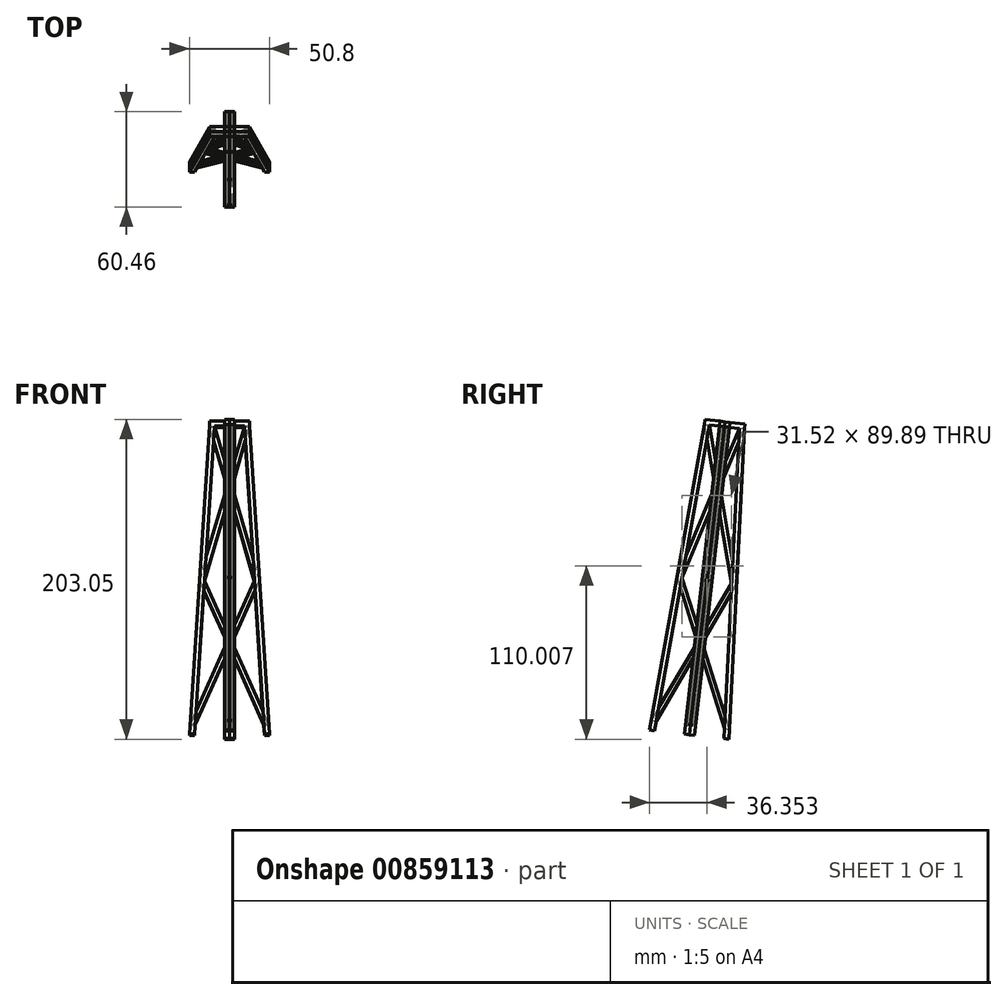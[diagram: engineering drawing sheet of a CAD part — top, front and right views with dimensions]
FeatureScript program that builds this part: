
annotation { "Feature Type Name" : "Feature", "Feature Type Description" : "" }
export const myFeature = defineFeature(function(context is Context, id is Id, definition is map)
    precondition{}
    {
        {
            var Q0;
            Q0=qCreatedBy(makeId("Top.planeOp"),FACE);
            var sketch = newSketch(context, id + "F0", { "sketchPlane" : qUnion([Q0])});
            skLineSegment(sketch, "E0", {"start": v(0, 0) * mm, "end": v(0, 116.82) * mm, "construction": true});
            skLineSegment(sketch, "E1", {"start": v(0, 0) * mm, "end": v(-140.82, 0) * mm, "construction": true});
            skSolve(sketch);
        }
        {
            var Q0;
            Q0=qCreatedBy(makeId("Right.planeOp"),FACE);
            var sketch = newSketch(context, id + "F1", { "sketchPlane" : qUnion([Q0])});
            skLineSegment(sketch, "E2", {"start": v(0, 0) * mm, "end": v(0, 190.5) * mm, "construction": true});
            skSolve(sketch);
        }
        {
            var Q0;
            Q0=qCreatedBy(makeId("Right.planeOp"),FACE);
            var sketch = newSketch(context, id + "F2", { "sketchPlane" : qUnion([Q0])});
            skPoint(sketch, "E3", {"position": v(-25.4, 0) * mm});
            skPoint(sketch, "E4.MirrorP", {"position": v(25.4, 0) * mm});
            skPoint(sketch, "E5", {"position": v(0, 215.9) * mm});
            skLineSegment(sketch, "E6", {"start": v(-25.4, 0) * mm, "end": v(0, 223.32) * mm, "construction": true});
            skSolve(sketch);
        }
        {
            var Q0;
            Q0 = qBodyType(qCreatedBy(id + "F2" ,EDGE), BodyType.WIRE);
            cPlane(context, id + "F3", {"entities" : qUnion([Q0]), "cplaneType" : CPlaneType.LINE_ANGLE, "offset" : 25.4 * mm, "angle" : 90 * degree, "oppositeDirection" : true, "width" : 152.4 * mm, "height" : 152.4 * mm});
        }
        {
            var Q0;
            Q0=qCreatedBy(id+"F3.planeOp",FACE);
            var sketch = newSketch(context, id + "F4", { "sketchPlane" : qUnion([Q0])});
            skPoint(sketch, "E7", {"position": v(-25.4, 0) * mm});
            skPoint(sketch, "E8", {"position": v(0, 215.9) * mm});
            skPoint(sketch, "E9", {"position": v(0, 196.85) * mm});
            skLineSegment(sketch, "E10", {"start": v(-25.4, 0) * mm, "end": v(-12.7, 196.85) * mm});
            skLineSegment(sketch, "E11.0", {"start": v(-22.22, 0) * mm, "end": v(-9.52, 196.85) * mm});
            skLineSegment(sketch, "E12", {"start": v(-25.4, 0) * mm, "end": v(-22.22, 0) * mm});
            skLineSegment(sketch, "E13", {"start": v(-12.7, 196.85) * mm, "end": v(-9.52, 196.85) * mm});
            skLineSegment(sketch, "E14", {"start": v(-12.7, 200.03) * mm, "end": v(-12.7, 196.85) * mm});
            skLineSegment(sketch, "E15.MirrorCS", {"start": v(12.7, 196.85) * mm, "end": v(9.52, 196.85) * mm});
            skLineSegment(sketch, "E16.MirrorCS", {"start": v(12.7, 200.03) * mm, "end": v(12.7, 196.85) * mm});
            skLineSegment(sketch, "E17.MirrorCS", {"start": v(25.4, 0) * mm, "end": v(22.22, 0) * mm});
            skLineSegment(sketch, "E18.MirrorCS", {"start": v(25.4, 0) * mm, "end": v(12.7, 196.85) * mm});
            skLineSegment(sketch, "E19.MirrorCS", {"start": v(22.22, 0) * mm, "end": v(9.52, 196.85) * mm});
            skLineSegment(sketch, "E20", {"start": v(-12.7, 196.85) * mm, "end": v(12.7, 196.85) * mm});
            skLineSegment(sketch, "E21", {"start": v(-12.7, 200.03) * mm, "end": v(12.7, 200.03) * mm});
            skLineSegment(sketch, "E22", {"start": v(-65.08, 200.03) * mm, "end": v(-65.08, 0) * mm, "construction": true});
            skLineSegment(sketch, "E23", {"start": v(-59.43, 196.85) * mm, "end": v(-59.43, 0) * mm, "construction": true});
            skLineSegment(sketch, "E24", {"start": v(-59.43, 98.43) * mm, "end": v(114.07, 98.43) * mm, "construction": true});
            skLineSegment(sketch, "E25", {"start": v(-44.46, 6.35) * mm, "end": v(-44.46, 0) * mm, "construction": true});
            skLineSegment(sketch, "E26", {"start": v(-25, 6.35) * mm, "end": v(15.87, 98.43) * mm});
            skLineSegment(sketch, "E27", {"start": v(15.87, 98.43) * mm, "end": v(19.05, 98.43) * mm});
            skLineSegment(sketch, "E28", {"start": v(19.05, 98.42) * mm, "end": v(-21.8, 6.35) * mm});
            skLineSegment(sketch, "E29", {"start": v(-21.8, 6.35) * mm, "end": v(-25, 6.35) * mm});
            skLineSegment(sketch, "E30", {"start": v(-9.52, 196.85) * mm, "end": v(19.05, 98.42) * mm});
            skLineSegment(sketch, "E31", {"start": v(15.87, 98.43) * mm, "end": v(-12.7, 196.85) * mm});
            skLineSegment(sketch, "E32", {"start": v(9.52, 196.85) * mm, "end": v(-19.05, 98.43) * mm});
            skLineSegment(sketch, "E33", {"start": v(-19.05, 98.43) * mm, "end": v(-15.88, 98.22) * mm});
            skLineSegment(sketch, "E34", {"start": v(-15.88, 98.22) * mm, "end": v(12.7, 196.85) * mm});
            skLineSegment(sketch, "E35", {"start": v(21.8, 6.35) * mm, "end": v(-19.05, 98.43) * mm});
            skLineSegment(sketch, "E36", {"start": v(-15.88, 98.22) * mm, "end": v(25, 6.35) * mm});
            skLineSegment(sketch, "E37", {"start": v(25, 6.35) * mm, "end": v(21.8, 6.35) * mm});
            skSolve(sketch);
        }
        {
            var Q0;
            {var subQ2=sQuery(id+"F4.wireOp",EDGE,"E12");Q0=makeQuery(id+"F4.imprint","IMPRINT",FACE,{"disambiguationData":[TD([[makeQuery(id+"F4.imprint","IMPRINT",EDGE,{"derivedFrom":subQ2}),1.0]])]});}
            var Q1;
            {var subQ0=sQuery(id+"F4.wireOp",EDGE,"E17.MirrorCS");Q1=makeQuery(id+"F4.imprint","IMPRINT",FACE,{"disambiguationData":[TD([[makeQuery(id+"F4.imprint","IMPRINT",EDGE,{"derivedFrom":subQ0}),-1.0]])]});}
            var Q2;
            {var subQ3=sQuery(id+"F4.wireOp",EDGE,"E26");var subQ5=sQuery(id+"F4.wireOp",EDGE,"E11.0");var subQ7=makeQuery(id+"F4.imprint","INTERSECT",VERTEX,{"derivedFrom":[subQ5,subQ3]});Q2=makeQuery(id+"F4.imprint","IMPRINT",FACE,{"disambiguationData":[TD([[makeQuery(id+"F4.imprint","IMPRINT",EDGE,{"disambiguationData":[TD([[subQ7,-1.0]])],"derivedFrom":subQ5}),1.0]])]});}
            var Q3;
            {var subQ0=sQuery(id+"F4.wireOp",EDGE,"E32");var subQ5=sQuery(id+"F4.wireOp",EDGE,"E11.0");var subQ6=makeQuery(id+"F4.imprint","INTERSECT",VERTEX,{"derivedFrom":[subQ5,subQ0]});Q3=makeQuery(id+"F4.imprint","IMPRINT",FACE,{"disambiguationData":[TD([[makeQuery(id+"F4.imprint","IMPRINT",EDGE,{"disambiguationData":[TD([[subQ6,-1.0]])],"derivedFrom":subQ5}),1.0]])]});}
            var Q4;
            {var subQ3=sQuery(id+"F4.wireOp",EDGE,"E29");Q4=makeQuery(id+"F4.imprint","IMPRINT",FACE,{"disambiguationData":[TD([[makeQuery(id+"F4.imprint","IMPRINT",EDGE,{"derivedFrom":subQ3}),-1.0]])]});}
            var Q5;
            {var subQ0=sQuery(id+"F4.wireOp",EDGE,"E33");Q5=makeQuery(id+"F4.imprint","IMPRINT",FACE,{"disambiguationData":[TD([[makeQuery(id+"F4.imprint","IMPRINT",EDGE,{"derivedFrom":subQ0}),-1.0]])]});}
            var Q6;
            {var subQ0=sQuery(id+"F4.wireOp",EDGE,"E33");Q6=makeQuery(id+"F4.imprint","IMPRINT",FACE,{"disambiguationData":[TD([[makeQuery(id+"F4.imprint","IMPRINT",EDGE,{"derivedFrom":subQ0}),1.0]])]});}
            var Q7;
            {var subQ5=sQuery(id+"F4.wireOp",EDGE,"E13");Q7=makeQuery(id+"F4.imprint","IMPRINT",FACE,{"disambiguationData":[TD([[makeQuery(id+"F4.imprint","IMPRINT",EDGE,{"derivedFrom":subQ5}),-1.0]])]});}
            var Q8;
            {var subQ3=sQuery(id+"F4.wireOp",EDGE,"E36");var subQ5=sQuery(id+"F4.wireOp",EDGE,"E19.MirrorCS");var subQ6=makeQuery(id+"F4.imprint","INTERSECT",VERTEX,{"derivedFrom":[subQ5,subQ3]});Q8=makeQuery(id+"F4.imprint","IMPRINT",FACE,{"disambiguationData":[TD([[makeQuery(id+"F4.imprint","IMPRINT",EDGE,{"disambiguationData":[TD([[subQ6,-1.0]])],"derivedFrom":subQ5}),-1.0]])]});}
            var Q9;
            {var subQ3=sQuery(id+"F4.wireOp",EDGE,"E30");var subQ5=sQuery(id+"F4.wireOp",EDGE,"E19.MirrorCS");var subQ6=makeQuery(id+"F4.imprint","INTERSECT",VERTEX,{"derivedFrom":[subQ5,subQ3]});Q9=makeQuery(id+"F4.imprint","IMPRINT",FACE,{"disambiguationData":[TD([[makeQuery(id+"F4.imprint","IMPRINT",EDGE,{"disambiguationData":[TD([[subQ6,-1.0]])],"derivedFrom":subQ5}),-1.0]])]});}
            var Q10;
            {var subQ3=sQuery(id+"F4.wireOp",EDGE,"E37");Q10=makeQuery(id+"F4.imprint","IMPRINT",FACE,{"disambiguationData":[TD([[makeQuery(id+"F4.imprint","IMPRINT",EDGE,{"derivedFrom":subQ3}),-1.0]])]});}
            var Q11;
            {var subQ0=sQuery(id+"F4.wireOp",EDGE,"E27");Q11=makeQuery(id+"F4.imprint","IMPRINT",FACE,{"disambiguationData":[TD([[makeQuery(id+"F4.imprint","IMPRINT",EDGE,{"derivedFrom":subQ0}),-1.0]])]});}
            var Q12;
            {var subQ0=sQuery(id+"F4.wireOp",EDGE,"E27");Q12=makeQuery(id+"F4.imprint","IMPRINT",FACE,{"disambiguationData":[TD([[makeQuery(id+"F4.imprint","IMPRINT",EDGE,{"derivedFrom":subQ0}),1.0]])]});}
            var Q13;
            {var subQ1=sQuery(id+"F4.wireOp",EDGE,"E13");Q13=makeQuery(id+"F4.imprint","IMPRINT",FACE,{"disambiguationData":[TD([[makeQuery(id+"F4.imprint","IMPRINT",EDGE,{"derivedFrom":subQ1}),1.0]])]});}
            var Q14;
            {var subQ0=sQuery(id+"F4.wireOp",EDGE,"E15.MirrorCS");Q14=makeQuery(id+"F4.imprint","IMPRINT",FACE,{"disambiguationData":[TD([[makeQuery(id+"F4.imprint","IMPRINT",EDGE,{"derivedFrom":subQ0}),1.0]])]});}
            extrude(context, id + "F5", {"entities" : qUnion([Q0, Q1, Q2, Q3, Q4, Q5, Q6, Q7, Q8, Q9, Q10, Q11, Q12, Q13, Q14]), "oppositeDirection" : true, "depth" : 3.17 * mm, "offsetDistance" : 25.4 * mm});
        }
        {
            var Q0;
            {var subQ5=sQuery(id+"F4.wireOp",EDGE,"E13");Q0=makeQuery(id+"F4.imprint","IMPRINT",FACE,{"disambiguationData":[TD([[makeQuery(id+"F4.imprint","IMPRINT",EDGE,{"derivedFrom":subQ5}),-1.0]])]});}
            var Q1;
            {var subQ3=sQuery(id+"F4.wireOp",EDGE,"E31");var subQ5=sQuery(id+"F4.wireOp",EDGE,"E32");var subQ6=makeQuery(id+"F4.imprint","INTERSECT",VERTEX,{"derivedFrom":[subQ3,subQ5]});Q1=makeQuery(id+"F4.imprint","IMPRINT",FACE,{"disambiguationData":[TD([[makeQuery(id+"F4.imprint","IMPRINT",EDGE,{"disambiguationData":[TD([[subQ6,-1.0]])],"derivedFrom":subQ3}),-1.0]])]});}
            var Q2;
            {var subQ0=sQuery(id+"F4.wireOp",EDGE,"E32");var subQ1=sQuery(id+"F4.wireOp",EDGE,"E19.MirrorCS");var subQ2=makeQuery(id+"F4.imprint","INTERSECT",VERTEX,{"derivedFrom":[subQ1,subQ0]});Q2=makeQuery(id+"F4.imprint","IMPRINT",FACE,{"disambiguationData":[TD([[makeQuery(id+"F4.imprint","IMPRINT",EDGE,{"disambiguationData":[TD([[subQ2,1.0]])],"derivedFrom":subQ1}),1.0]])]});}
            var Q3;
            {var subQ0=sQuery(id+"F4.wireOp",EDGE,"E15.MirrorCS");Q3=makeQuery(id+"F4.imprint","IMPRINT",FACE,{"disambiguationData":[TD([[makeQuery(id+"F4.imprint","IMPRINT",EDGE,{"derivedFrom":subQ0}),1.0]])]});}
            var Q4;
            {var subQ0=sQuery(id+"F4.wireOp",EDGE,"E34");var subQ1=sQuery(id+"F4.wireOp",EDGE,"E30");var subQ2=makeQuery(id+"F4.imprint","INTERSECT",VERTEX,{"derivedFrom":[subQ1,subQ0]});Q4=makeQuery(id+"F4.imprint","IMPRINT",FACE,{"disambiguationData":[TD([[makeQuery(id+"F4.imprint","IMPRINT",EDGE,{"disambiguationData":[TD([[subQ2,1.0]])],"derivedFrom":subQ1}),-1.0]])]});}
            var Q5;
            {var subQ3=sQuery(id+"F4.wireOp",EDGE,"E32");var subQ5=sQuery(id+"F4.wireOp",EDGE,"E31");var subQ7=makeQuery(id+"F4.imprint","INTERSECT",VERTEX,{"derivedFrom":[subQ5,subQ3]});Q5=makeQuery(id+"F4.imprint","IMPRINT",FACE,{"disambiguationData":[TD([[makeQuery(id+"F4.imprint","IMPRINT",EDGE,{"disambiguationData":[TD([[subQ7,1.0]])],"derivedFrom":subQ5}),1.0]])]});}
            var Q6;
            {var subQ0=sQuery(id+"F4.wireOp",EDGE,"E33");Q6=makeQuery(id+"F4.imprint","IMPRINT",FACE,{"disambiguationData":[TD([[makeQuery(id+"F4.imprint","IMPRINT",EDGE,{"derivedFrom":subQ0}),1.0]])]});}
            var Q7;
            {var subQ3=sQuery(id+"F4.wireOp",EDGE,"E30");var subQ5=sQuery(id+"F4.wireOp",EDGE,"E34");var subQ6=makeQuery(id+"F4.imprint","INTERSECT",VERTEX,{"derivedFrom":[subQ3,subQ5]});Q7=makeQuery(id+"F4.imprint","IMPRINT",FACE,{"disambiguationData":[TD([[makeQuery(id+"F4.imprint","IMPRINT",EDGE,{"disambiguationData":[TD([[subQ6,-1.0]])],"derivedFrom":subQ3}),-1.0]])]});}
            var Q8;
            {var subQ0=sQuery(id+"F4.wireOp",EDGE,"E27");Q8=makeQuery(id+"F4.imprint","IMPRINT",FACE,{"disambiguationData":[TD([[makeQuery(id+"F4.imprint","IMPRINT",EDGE,{"derivedFrom":subQ0}),1.0]])]});}
            var Q9;
            {var subQ3=sQuery(id+"F4.wireOp",EDGE,"E28");var subQ5=sQuery(id+"F4.wireOp",EDGE,"E36");var subQ7=makeQuery(id+"F4.imprint","INTERSECT",VERTEX,{"derivedFrom":[subQ3,subQ5]});Q9=makeQuery(id+"F4.imprint","IMPRINT",FACE,{"disambiguationData":[TD([[makeQuery(id+"F4.imprint","IMPRINT",EDGE,{"disambiguationData":[TD([[subQ7,1.0]])],"derivedFrom":subQ3}),-1.0]])]});}
            var Q10;
            {var subQ0=sQuery(id+"F4.wireOp",EDGE,"E27");Q10=makeQuery(id+"F4.imprint","IMPRINT",FACE,{"disambiguationData":[TD([[makeQuery(id+"F4.imprint","IMPRINT",EDGE,{"derivedFrom":subQ0}),-1.0]])]});}
            var Q11;
            {var subQ0=sQuery(id+"F4.wireOp",EDGE,"E36");var subQ5=sQuery(id+"F4.wireOp",EDGE,"E26");var subQ6=makeQuery(id+"F4.imprint","INTERSECT",VERTEX,{"derivedFrom":[subQ5,subQ0]});Q11=makeQuery(id+"F4.imprint","IMPRINT",FACE,{"disambiguationData":[TD([[makeQuery(id+"F4.imprint","IMPRINT",EDGE,{"disambiguationData":[TD([[subQ6,1.0]])],"derivedFrom":subQ5}),1.0]])]});}
            var Q12;
            {var subQ0=sQuery(id+"F4.wireOp",EDGE,"E33");Q12=makeQuery(id+"F4.imprint","IMPRINT",FACE,{"disambiguationData":[TD([[makeQuery(id+"F4.imprint","IMPRINT",EDGE,{"derivedFrom":subQ0}),-1.0]])]});}
            var Q13;
            {var subQ0=sQuery(id+"F4.wireOp",EDGE,"E36");var subQ1=sQuery(id+"F4.wireOp",EDGE,"E26");var subQ2=makeQuery(id+"F4.imprint","INTERSECT",VERTEX,{"derivedFrom":[subQ1,subQ0]});Q13=makeQuery(id+"F4.imprint","IMPRINT",FACE,{"disambiguationData":[TD([[makeQuery(id+"F4.imprint","IMPRINT",EDGE,{"disambiguationData":[TD([[subQ2,1.0]])],"derivedFrom":subQ1}),-1.0]])]});}
            var Q14;
            {var subQ3=sQuery(id+"F4.wireOp",EDGE,"E35");var subQ5=sQuery(id+"F4.wireOp",EDGE,"E28");var subQ7=makeQuery(id+"F4.imprint","INTERSECT",VERTEX,{"derivedFrom":[subQ5,subQ3]});Q14=makeQuery(id+"F4.imprint","IMPRINT",FACE,{"disambiguationData":[TD([[makeQuery(id+"F4.imprint","IMPRINT",EDGE,{"disambiguationData":[TD([[subQ7,1.0]])],"derivedFrom":subQ5}),1.0]])]});}
            var Q15;
            {var subQ0=sQuery(id+"F4.wireOp",EDGE,"E26");var subQ1=sQuery(id+"F4.wireOp",EDGE,"E11.0");var subQ2=makeQuery(id+"F4.imprint","INTERSECT",VERTEX,{"derivedFrom":[subQ1,subQ0]});Q15=makeQuery(id+"F4.imprint","IMPRINT",FACE,{"disambiguationData":[TD([[makeQuery(id+"F4.imprint","IMPRINT",EDGE,{"disambiguationData":[TD([[subQ2,-1.0]])],"derivedFrom":subQ0}),-1.0]])]});}
            var Q16;
            {var subQ3=sQuery(id+"F4.wireOp",EDGE,"E37");Q16=makeQuery(id+"F4.imprint","IMPRINT",FACE,{"disambiguationData":[TD([[makeQuery(id+"F4.imprint","IMPRINT",EDGE,{"derivedFrom":subQ3}),-1.0]])]});}
            var Q17;
            {var subQ3=sQuery(id+"F4.wireOp",EDGE,"E29");Q17=makeQuery(id+"F4.imprint","IMPRINT",FACE,{"disambiguationData":[TD([[makeQuery(id+"F4.imprint","IMPRINT",EDGE,{"derivedFrom":subQ3}),-1.0]])]});}
            extrude(context, id + "F6", {"entities" : qUnion([Q0, Q1, Q2, Q3, Q4, Q5, Q6, Q7, Q8, Q9, Q10, Q11, Q12, Q13, Q14, Q15, Q16, Q17]), "operationType" : NewBodyOperationType.ADD, "depth" : 1.59 * mm, "offsetDistance" : 25.4 * mm});
        }
        {
            var Q0;
            Q0=makeQuery(id+"F5.opExtrude","SWEPT_BODY",BODY,{"disambiguationData":[OSD([sQuery(id+"F4.wireOp",EDGE,"E10"),sQuery(id+"F4.wireOp",EDGE,"E11.0"),sQuery(id+"F4.wireOp",EDGE,"E12"),sQuery(id+"F4.wireOp",EDGE,"E14"),sQuery(id+"F4.wireOp",EDGE,"E16.MirrorCS"),sQuery(id+"F4.wireOp",EDGE,"E17.MirrorCS"),sQuery(id+"F4.wireOp",EDGE,"E18.MirrorCS"),sQuery(id+"F4.wireOp",EDGE,"E19.MirrorCS"),sQuery(id+"F4.wireOp",EDGE,"E20"),sQuery(id+"F4.wireOp",EDGE,"E21"),sQuery(id+"F4.wireOp",EDGE,"E32")])]});
            var Q1;
            Q1=sQuery(id+"F2.wireOp",EDGE,"E6");
            circularPattern(context, id + "F7", {"entities" : qUnion([Q0]), "axis" : qUnion([Q1]), "angle" : 360 * degree, "instanceCount" : 4, "equalSpace" : true});
        }
    });
